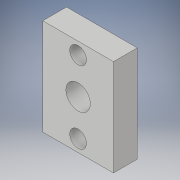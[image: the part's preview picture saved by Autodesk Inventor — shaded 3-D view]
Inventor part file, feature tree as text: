
AUTODESK INVENTOR PART (.ipt)
format: ipt  version: 2019 (Build 230136000, 136)  size: 120,832 bytes
history: native  units: in
note: dims shown in document units (in); Inventor stores cm internally (conversion verified against a paired STEP export)
features: sketch x3, hole x2, projected_geometry x2, extrude x1
ambient origin geometry x8: Origin, YZ Plane, XZ Plane, XY Plane, X Axis, Y Axis, Z Axis, Center Point
bodies: Solid1 (feature_tree)
feature tree (8):
  extrude  "Extrusion1"  Depth=1.5in
  hole  "Hole1"  [1 undecoded]
  hole  "Hole2"  [1 undecoded]
  sketch  "Sketch1"  dims[d0=1.1in d1=1.5in]
  sketch  "Sketch2"  dims[d2=0.37in d3=0.0in d4=1.125in]
  projected_geometry  "Projected Loop1"
  sketch  "Sketch3"  dims[d5=1.5in d6=0.1875in d7=1.1in d8=0.55in d9=0.55in d10=0.26in d11=0.75in d12=0.375in d13=0.25in d14=0.5635in d15=0.432in d16=0.8108in d17=1.1in d18=1.5in d19=0.55in d20=0.75in d21=0.38in d22=0.75in d23=0.375in d24=0.25in d25=0.5635in d26=0.432in d27=0.8108in]
  projected_geometry  "Projected Loop2"
note: 2 required parameter values undecoded (feature->parameter linkage not recoverable at this tier; creation-order binding heuristic only, values carry confidence <= 0.55)
